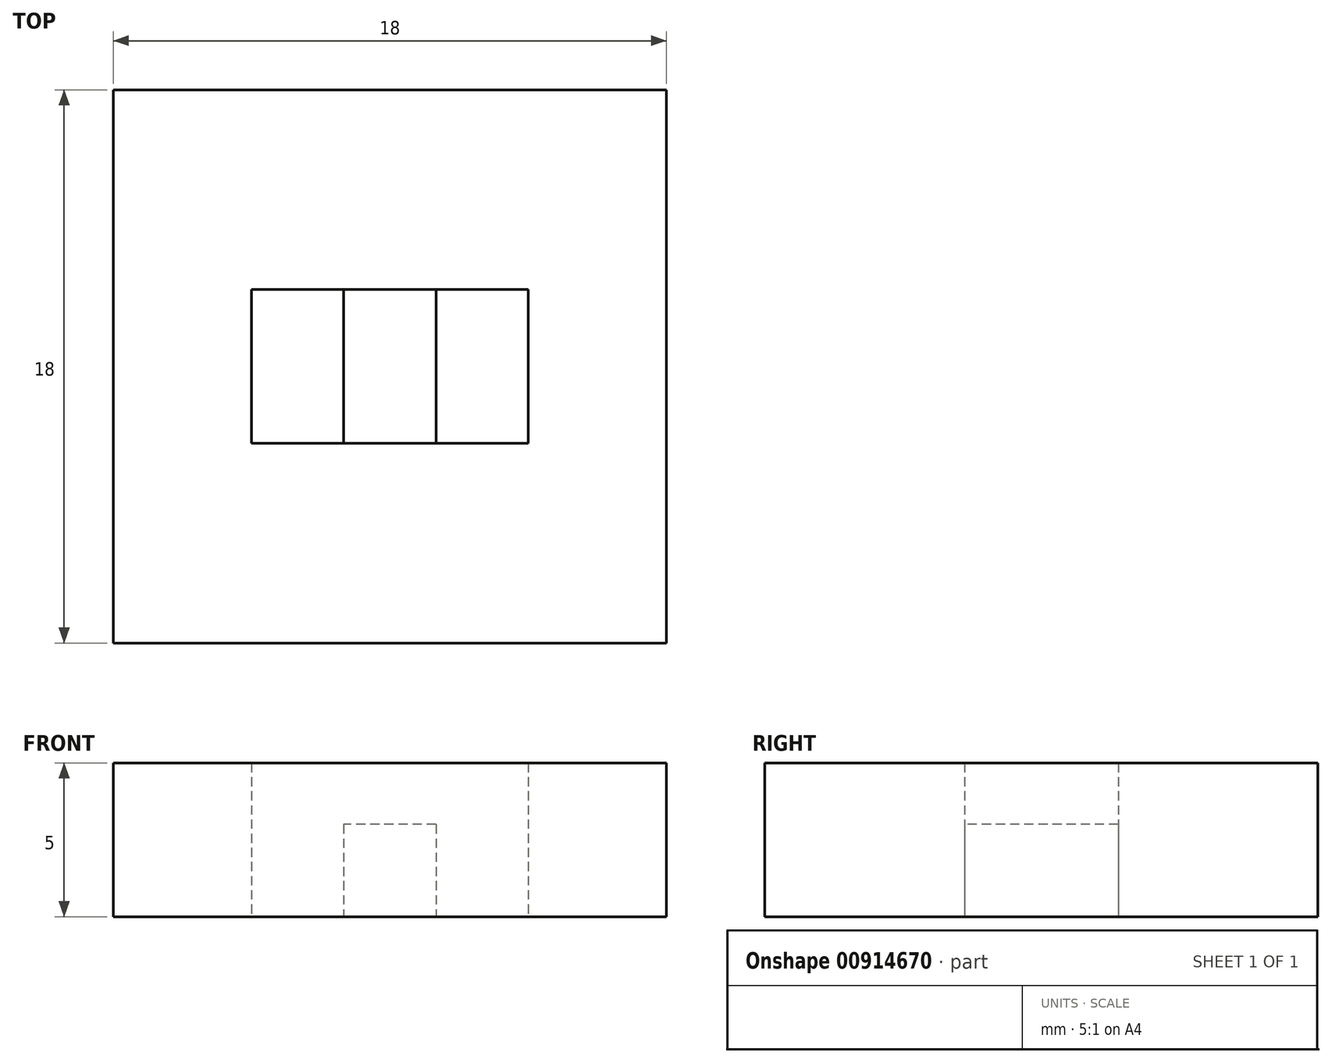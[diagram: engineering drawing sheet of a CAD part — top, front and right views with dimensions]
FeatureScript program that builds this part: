
annotation { "Feature Type Name" : "Feature", "Feature Type Description" : "" }
export const myFeature = defineFeature(function(context is Context, id is Id, definition is map)
    precondition{}
    {
        {
            var Q0;
            Q0=qCreatedBy(makeId("Top.planeOp"),FACE);
            var sketch = newSketch(context, id + "F0", { "sketchPlane" : qUnion([Q0])});
            skLineSegment(sketch, "E0.bottom", {"start": v(9, 9) * mm, "end": v(-9, 9) * mm});
            skLineSegment(sketch, "E0.top", {"start": v(9, -9) * mm, "end": v(-9, -9) * mm});
            skLineSegment(sketch, "E0.left", {"start": v(9, 9) * mm, "end": v(9, -9) * mm});
            skLineSegment(sketch, "E0.right", {"start": v(-9, 9) * mm, "end": v(-9, -9) * mm});
            skPoint(sketch, "E0.middle", {"position": v(0, 0) * mm});
            skLineSegment(sketch, "E1.bottom", {"start": v(4.5, 2.5) * mm, "end": v(-4.5, 2.5) * mm});
            skLineSegment(sketch, "E1.top", {"start": v(4.5, -2.5) * mm, "end": v(-4.5, -2.5) * mm});
            skLineSegment(sketch, "E1.left", {"start": v(4.5, 2.5) * mm, "end": v(4.5, -2.5) * mm});
            skLineSegment(sketch, "E1.right", {"start": v(-4.5, 2.5) * mm, "end": v(-4.5, -2.5) * mm});
            skLineSegment(sketch, "E2.bottom", {"start": v(1.5, 2.5) * mm, "end": v(-1.5, 2.5) * mm});
            skLineSegment(sketch, "E2.top", {"start": v(1.5, -2.5) * mm, "end": v(-1.5, -2.5) * mm});
            skLineSegment(sketch, "E2.left", {"start": v(1.5, 2.5) * mm, "end": v(1.5, -2.5) * mm});
            skLineSegment(sketch, "E2.right", {"start": v(-1.5, 2.5) * mm, "end": v(-1.5, -2.5) * mm});
            skSolve(sketch);
        }
        {
            var Q0;
            Q0=makeQuery(id+"F0.imprint","IMPRINT",FACE,{"disambiguationData":[TD([[makeQuery(id+"F0.imprint","IMPRINT",EDGE,{"derivedFrom":sQuery(id+"F0.wireOp",EDGE,"E0.bottom")}),1.0]])]});
            var Q1;
            {var subQ2=sQuery(id+"F0.wireOp",EDGE,"E2.left");Q1=makeQuery(id+"F0.imprint","IMPRINT",FACE,{"disambiguationData":[TD([[makeQuery(id+"F0.imprint","IMPRINT",EDGE,{"derivedFrom":subQ2}),-1.0]])]});}
            extrude(context, id + "F1", {"entities" : qUnion([Q0, Q1]), "depth" : 5 * mm, "offsetDistance" : 25 * mm});
        }
        {
            var Q0;
            Q0=makeQuery(id+"F1.opExtrude","CAP_FACE",FACE,{"disambiguationData":[OSD([sQuery(id+"F0.wireOp",EDGE,"E0.bottom"),sQuery(id+"F0.wireOp",EDGE,"E0.top"),sQuery(id+"F0.wireOp",EDGE,"E0.left"),sQuery(id+"F0.wireOp",EDGE,"E0.right"),sQuery(id+"F0.wireOp",EDGE,"E1.bottom"),sQuery(id+"F0.wireOp",EDGE,"E1.top"),sQuery(id+"F0.wireOp",EDGE,"E1.left"),sQuery(id+"F0.wireOp",EDGE,"E1.right"),sQuery(id+"F0.wireOp",EDGE,"E2.left"),sQuery(id+"F0.wireOp",EDGE,"E2.right")])],"isStart":false});
            var sketch = newSketch(context, id + "F2", { "sketchPlane" : qUnion([Q0])});
            skLineSegment(sketch, "E3.bottom", {"start": v(1.5, 2.5) * mm, "end": v(-1.5, 2.5) * mm});
            skLineSegment(sketch, "E3.top", {"start": v(1.5, -2.5) * mm, "end": v(-1.5, -2.5) * mm});
            skLineSegment(sketch, "E3.left", {"start": v(1.5, 2.5) * mm, "end": v(1.5, -2.5) * mm});
            skLineSegment(sketch, "E3.right", {"start": v(-1.5, 2.5) * mm, "end": v(-1.5, -2.5) * mm});
            skPoint(sketch, "E3.middle", {"position": v(0, 0) * mm});
            skSolve(sketch);
        }
        {
            var Q0;
            Q0 = qSketchRegion(id + "F2", true);
            extrude(context, id + "F3", {"entities" : qUnion([Q0]), "operationType" : NewBodyOperationType.REMOVE, "oppositeDirection" : true, "depth" : 2 * mm, "offsetDistance" : 25 * mm});
        }
    });
